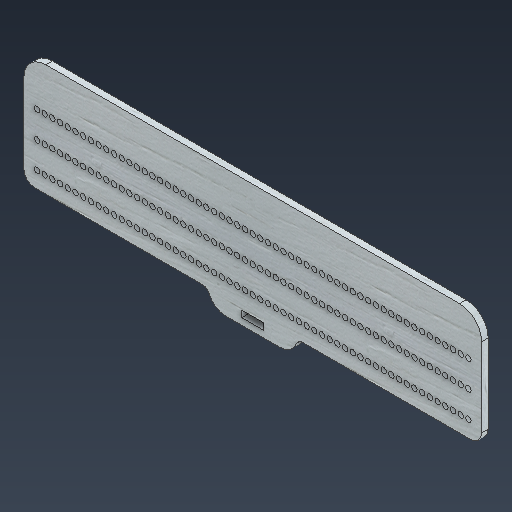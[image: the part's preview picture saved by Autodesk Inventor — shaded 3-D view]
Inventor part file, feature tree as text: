
AUTODESK INVENTOR PART (.ipt)
format: ipt  version: 2025.3 (Build 293356030, 356C)  size: 495,616 bytes
history: native  units: mm
features: other x3, sketch x2, extrude x1
ambient origin geometry x8: Origin, YZ Plane, XZ Plane, XY Plane, X Axis, Y Axis, Z Axis, Center Point
bodies: Body1 (feature_tree)
feature tree (6):
  other  "實體1"
  extrude  "擠出1"  Depth=10.0mm
  sketch  "草圖3"
  sketch  "草圖1"
  other  "草圖 - 矩形陣列5"
  other  "草圖 - 矩形陣列8"
